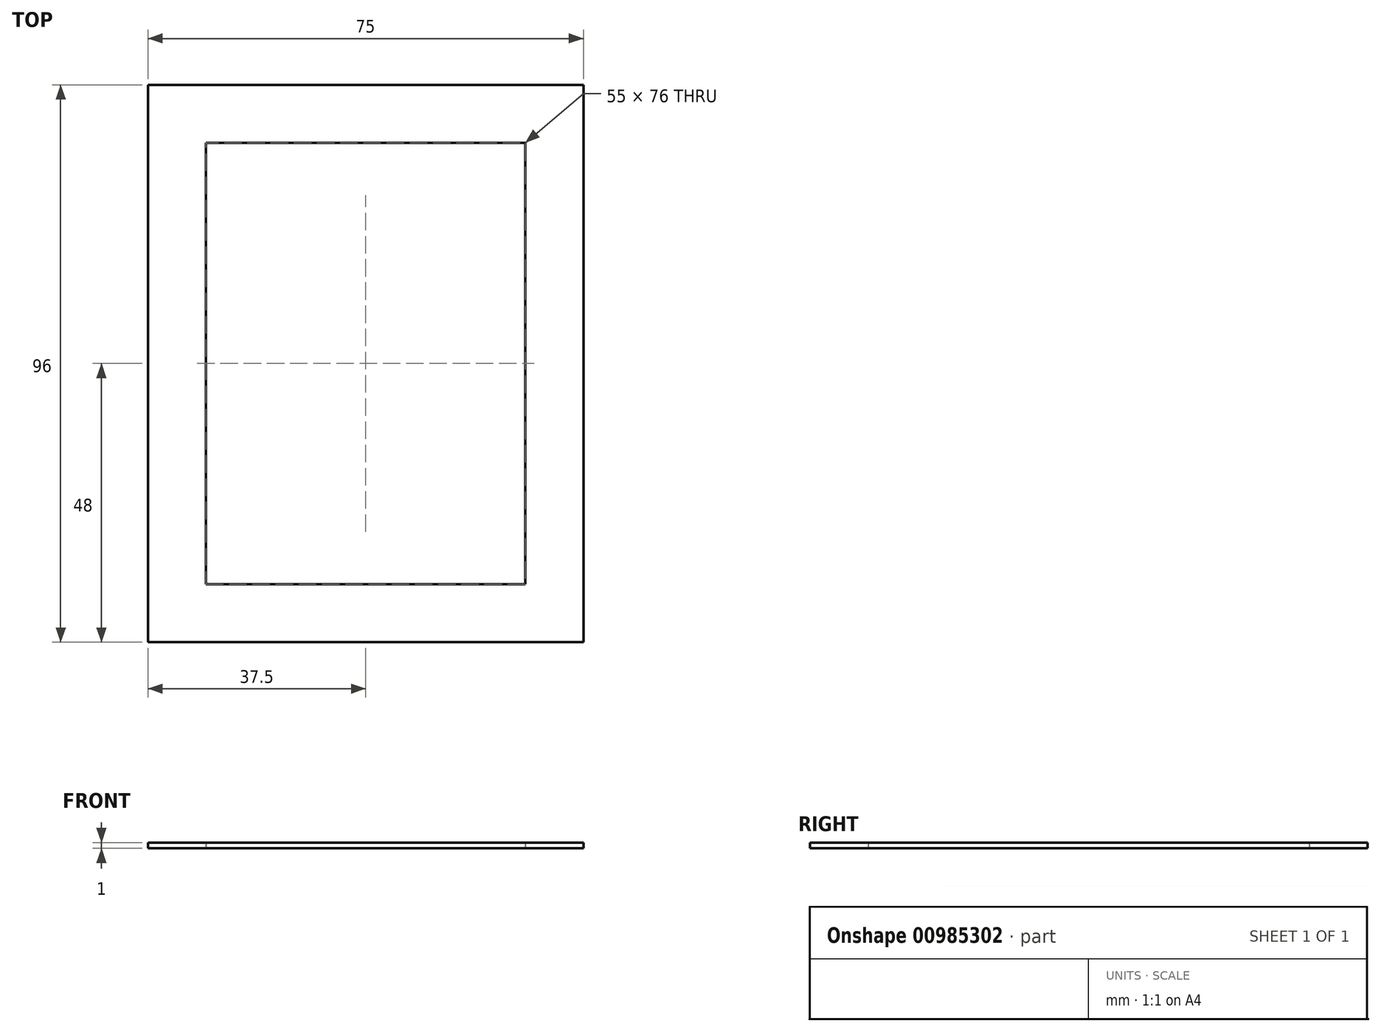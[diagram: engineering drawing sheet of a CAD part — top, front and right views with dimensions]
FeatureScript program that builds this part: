
annotation { "Feature Type Name" : "Feature", "Feature Type Description" : "" }
export const myFeature = defineFeature(function(context is Context, id is Id, definition is map)
    precondition{}
    {
        {
            var Q0;
            Q0=qCreatedBy(makeId("Top.planeOp"), FACE);
            var sketch = newSketch(context, id + "F0", { "sketchPlane" : qUnion([Q0])});
            skLineSegment(sketch, "E0.bottom", {"start": v(27.5, 38) * mm, "end": v(-27.5, 38) * mm});
            skLineSegment(sketch, "E0.top", {"start": v(27.5, -38) * mm, "end": v(-27.5, -38) * mm});
            skLineSegment(sketch, "E0.left", {"start": v(27.5, 38) * mm, "end": v(27.5, -38) * mm});
            skLineSegment(sketch, "E0.right", {"start": v(-27.5, 38) * mm, "end": v(-27.5, -38) * mm});
            skPoint(sketch, "E0.middle", {"position": v(0, 0) * mm});
            skLineSegment(sketch, "E1.bottom", {"start": v(37.5, 48) * mm, "end": v(-37.5, 48) * mm});
            skLineSegment(sketch, "E1.top", {"start": v(37.5, -48) * mm, "end": v(-37.5, -48) * mm});
            skLineSegment(sketch, "E1.left", {"start": v(37.5, 48) * mm, "end": v(37.5, -48) * mm});
            skLineSegment(sketch, "E1.right", {"start": v(-37.5, 48) * mm, "end": v(-37.5, -48) * mm});
            skSolve(sketch);
        }
        {
            var Q0;
            Q0 = qSketchRegion(id + "F0", true);
            extrude(context, id + "F1", {"entities" : qUnion([Q0]), "domain" : OperationDomain.MODEL, "flatOperationType" : FlatOperationType.REMOVE, "depth" : 1 * mm, "offsetDistance" : 25 * mm});
        }
    });
